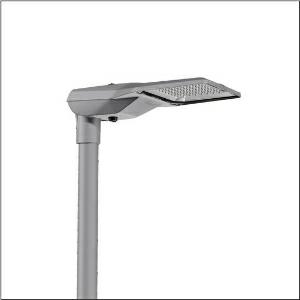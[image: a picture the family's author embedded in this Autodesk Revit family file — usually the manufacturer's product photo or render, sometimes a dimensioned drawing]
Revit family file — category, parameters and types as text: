
# Revit family: streetlight_sl_21_iq_midi___st1_0ab_5xe3m31y08mb_ceed
name_source: partatom
category: Lighting Fixtures
units: mm (PartAtom-declared; Revit-internal decimal feet)

## family parameters
Cut with Voids When Loaded = No
Host = Face
Light Source = No
Part Type = Normal
Room Calculation Point = No
Round Connector Dimension = Use Diameter
Shared = No

## types (1)
- --- (1 x LED, 16140 lm, 129.3 W, 3000K)
    Apparent Load = 129 VA
    CIE Flux Codes = 38 73 97 100 100
    Color Rendering = 70
    Color Temperature = 3000K
    Default Elevation = 1800 mm
    Description = Streetlight SL 21 iQ midi, mast luminaire, primary light control with lens, of PMMA, primary optical cover: cover, of toughened safety glass, transparent, light distribution: ST1.0aB, light emission: direct distribution, primary light characteristic: asymmetric, installation type: post-top, side-entry, LED, High Power LED, rated luminous flux: 16.140lm, luminous efficacy: 125lm/W, light colour: 730, colour temperature: 3000K, control gear: iQ-Street Remote, D4i with power reduction, control: pre-setting: logarithmic dimming characteristic, Street-Remote, Auto-Match, Temp-Guard, Lumen-Switch, Night-Set, Smart-Wire, Light-Fading, Desk-Remote (wireless, voltage-free reading and setting of iQ features in the workshop via application-optimized NFC function/RFID function), optimised constant luminous flux control (CLO 2.0), mains connection: 230..240V, AC, 50/60Hz, start of lifetime: 129W, end of service life: 142W, reduction: 56W, luminaire housing, of diecast aluminium, powder-coated, Siteco® metallic grey (DB 702S), corrosivity category C5 mid according to DIN EN ISO 12944, please order mast flange separately, inclination adjustable: 0°, 5°, 10°, 15°, sealing non-destructively replaceable, multi-level sealing system, length: 644mm, width: 335mm, height: 110mm, mast flange for spigot size: 42mm (side-entry): 5XC10008XM4, 60/48mm (side-entry/post-top): 5XC10108XM2, 76/60mm (side-entry/post-top): 5XC10108XM1, mounting height: 4..8m, Smart Interface below and above, protection rating (complete): IP66, insulation class (complete): insulation class II (safety insulation), certification: CE, ENEC, ENEC+, VDE, impact resistance: IK10, permissible operating ambient temperature for outdoor applications: -40..+50°C, standard-compliant lighting for roads and squares, packaging unit: 1 piece

Light Distribution: ST1.0aB
    Height = 111 mm
    Lamp = 1 x LED
    Lamp Light Flux = 16140 lm
    Lamp Power = 129.3 W
    Lamp count = 1
    Length = 644 mm
    Luminous efficacy = 125 lm/W
    Manufacturer = Siteco
    ModVariant = No
    Model = 5XE3M31Y08MB
    Number of Poles = 1
    OnlyDefault = Yes
    Power Factor = 1
    Product Name = Streetlight SL 21 iQ midi | ST1.0aB
    Product group = mast luminaire | pylon top
    ProductGroupID = 6100
    Protection Class = Protection class II
    Protection Degree = IP 66
    RLX_Detail_Level = 1
    RLX_Emergency_Light_Flux = 0 lm
    RLX_Emergency_Type = 0
    RLX_Emergency_Type_DB = No
    RlxData = <blob elided: 27201 chars, md5=887772c1>
    Socket = socket
    Standby Power = 0 W
    System Light Flux = 16141 lm
    System Power = 129 W
    Type Comments = factory setting: luminous flux: 100 % | dim-lin: 254 | 672 mA
    Type Image = l_1004304.jpg
    URL = http://relux.com
    VarID = @adj_112286
    Voltage = 0 V
    Weight = 0.00 kg
    Width = 336 mm

## geometry (parser evidence)
native form markers: Blend x4, Sweep x12
no freeform markers — native parametric forms only
